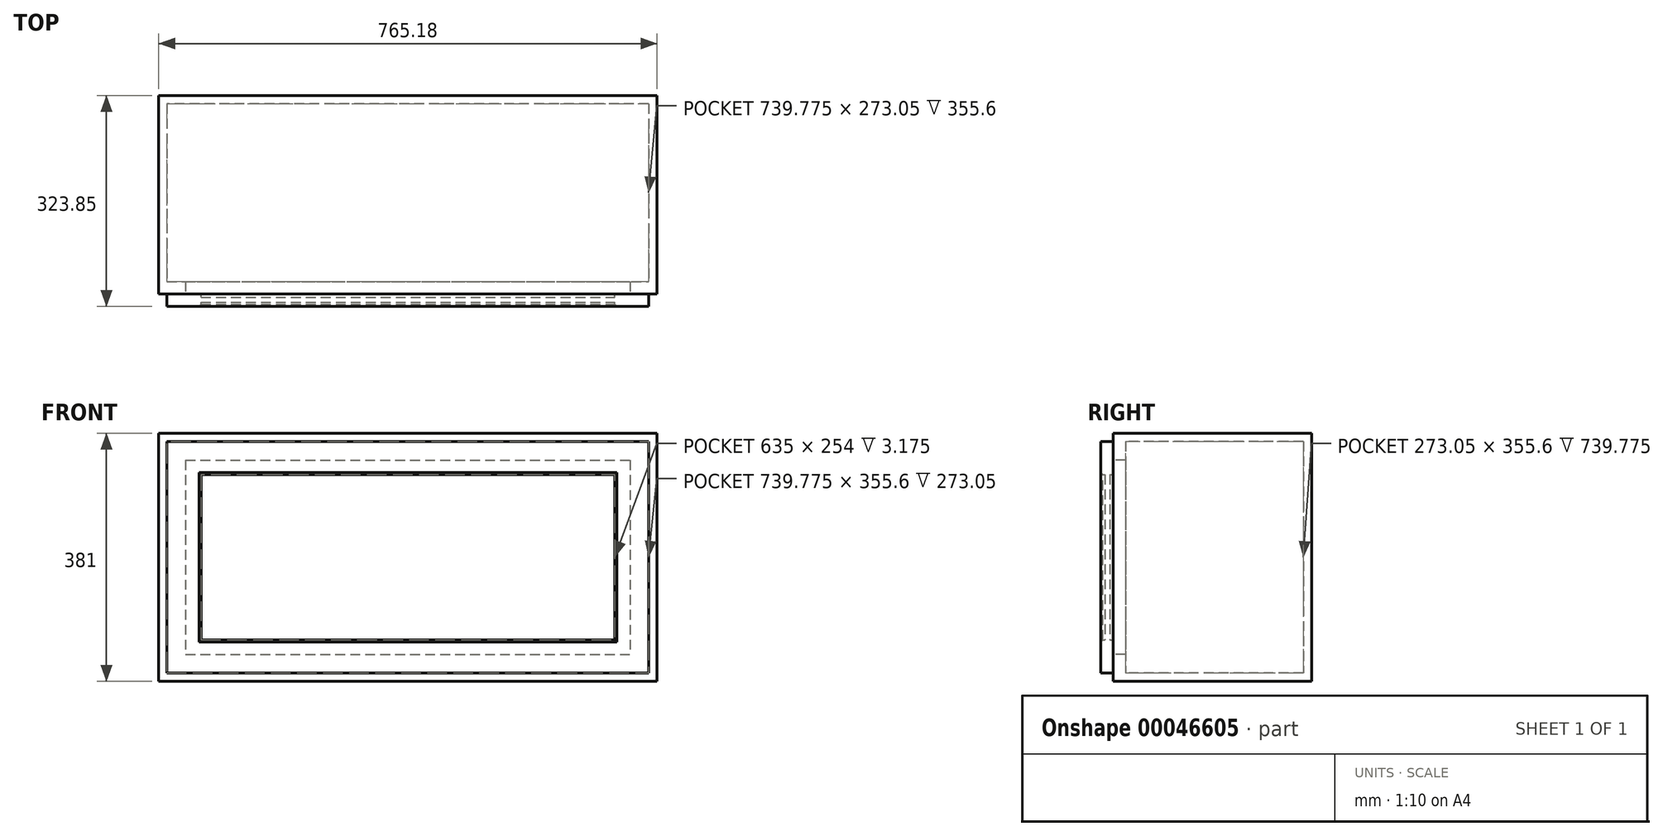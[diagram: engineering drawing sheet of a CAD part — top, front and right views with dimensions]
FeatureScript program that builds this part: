
annotation { "Feature Type Name" : "Feature", "Feature Type Description" : "" }
export const myFeature = defineFeature(function(context is Context, id is Id, definition is map)
    precondition{}
    {
        {
            var Q0;
            Q0=qCreatedBy(makeId("Top.planeOp"),FACE);
            var sketch = newSketch(context, id + "F0", { "sketchPlane" : qUnion([Q0])});
            skLineSegment(sketch, "E0.rect.bottom", {"start": v(382.59, 152.4) * mm, "end": v(-382.59, 152.4) * mm});
            skLineSegment(sketch, "E0.rect.top", {"start": v(382.59, -152.4) * mm, "end": v(-382.59, -152.4) * mm});
            skLineSegment(sketch, "E0.rect.left", {"start": v(382.59, 152.4) * mm, "end": v(382.59, -152.4) * mm});
            skLineSegment(sketch, "E0.rect.right", {"start": v(-382.59, 152.4) * mm, "end": v(-382.59, -152.4) * mm});
            skPoint(sketch, "E0.rect.middle", {"position": v(0, 0) * mm});
            skSolve(sketch);
        }
        {
            var Q0;
            Q0=qSketchRegion(id+"F0",true);
            extrude(context, id + "F1", {"entities" : qUnion([Q0]), "depth" : 381 * mm});
        }
        {
            var Q0;
            Q0=makeQuery(id+"F1.opExtrude","SWEPT_FACE",FACE,{"disambiguationData":[OSD([sQuery(id+"F0.wireOp",EDGE,"E0.rect.top")])]});
            shell(context, id + "F2", {"entities" : qUnion([Q0]), "thickness" : 12.7 * mm});
        }
        {
            var Q0;
            Q0=makeQuery(id+"F1.opExtrude","SWEPT_FACE",FACE,{"disambiguationData":[OSD([sQuery(id+"F0.wireOp",EDGE,"E0.rect.top")])]});
            var sketch = newSketch(context, id + "F3", { "sketchPlane" : qUnion([Q0])});
            skLineSegment(sketch, "E1", {"start": v(-382.59, 0) * mm, "end": v(382.59, 381) * mm, "construction": true});
            skLineSegment(sketch, "E2.rect.bottom", {"start": v(-317.5, 317.5) * mm, "end": v(317.5, 317.5) * mm});
            skLineSegment(sketch, "E2.rect.top", {"start": v(-317.5, 63.5) * mm, "end": v(317.5, 63.5) * mm});
            skLineSegment(sketch, "E2.rect.left", {"start": v(-317.5, 317.5) * mm, "end": v(-317.5, 63.5) * mm});
            skLineSegment(sketch, "E2.rect.right", {"start": v(317.5, 317.5) * mm, "end": v(317.5, 63.5) * mm});
            skPoint(sketch, "E2.rect.middle", {"position": v(0, 190.5) * mm});
            skLineSegment(sketch, "E3.rect.bottom", {"start": v(-341.31, 339.72) * mm, "end": v(341.31, 339.72) * mm});
            skLineSegment(sketch, "E3.rect.top", {"start": v(-341.31, 41.28) * mm, "end": v(341.31, 41.28) * mm});
            skLineSegment(sketch, "E3.rect.left", {"start": v(-341.31, 339.72) * mm, "end": v(-341.31, 41.28) * mm});
            skLineSegment(sketch, "E3.rect.right", {"start": v(341.31, 339.72) * mm, "end": v(341.31, 41.28) * mm});
            skLineSegment(sketch, "E4.rect.bottom", {"start": v(-382.59, 381) * mm, "end": v(382.59, 381) * mm});
            skLineSegment(sketch, "E4.rect.top", {"start": v(-382.59, 0) * mm, "end": v(382.59, 0) * mm});
            skLineSegment(sketch, "E4.rect.left", {"start": v(-382.59, 381) * mm, "end": v(-382.59, 0) * mm});
            skLineSegment(sketch, "E4.rect.right", {"start": v(382.59, 381) * mm, "end": v(382.59, 0) * mm});
            skLineSegment(sketch, "E5.rect.bottom", {"start": v(-374.65, 374.65) * mm, "end": v(374.65, 374.65) * mm});
            skLineSegment(sketch, "E5.rect.top", {"start": v(-374.65, 6.35) * mm, "end": v(374.65, 6.35) * mm});
            skLineSegment(sketch, "E5.rect.left", {"start": v(-374.65, 374.65) * mm, "end": v(-374.65, 6.35) * mm});
            skLineSegment(sketch, "E5.rect.right", {"start": v(374.65, 374.65) * mm, "end": v(374.65, 6.35) * mm});
            skSolve(sketch);
        }
        {
            var Q0;
            Q0=makeQuery(id+"F3.imprint","IMPRINT",FACE,{"disambiguationData":[TD([[makeQuery(id+"F3.imprint","IMPRINT",EDGE,{"derivedFrom":sQuery(id+"F3.wireOp",EDGE,"E4.rect.bottom")}),1.0]])]});
            var Q1;
            Q1=makeQuery(id+"F3.imprint","IMPRINT",FACE,{"disambiguationData":[TD([[makeQuery(id+"F3.imprint","IMPRINT",EDGE,{"derivedFrom":sQuery(id+"F3.wireOp",EDGE,"E5.rect.bottom")}),-1.0]])]});
            var Q2;
            Q2=makeQuery(id+"F3.imprint","IMPRINT",FACE,{"disambiguationData":[TD([[makeQuery(id+"F3.imprint","IMPRINT",EDGE,{"derivedFrom":sQuery(id+"F3.wireOp",EDGE,"E3.rect.bottom")}),1.0]])]});
            extrude(context, id + "F4", {"entities" : qUnion([Q0, Q1, Q2]), "operationType" : NewBodyOperationType.ADD, "oppositeDirection" : true, "depth" : 19.05 * mm});
        }
        {
            var Q0;
            Q0=makeQuery(id+"F3.imprint","IMPRINT",FACE,{"disambiguationData":[TD([[makeQuery(id+"F3.imprint","IMPRINT",EDGE,{"derivedFrom":sQuery(id+"F3.wireOp",EDGE,"E3.rect.bottom")}),1.0]])]});
            var Q1;
            Q1=makeQuery(id+"F3.imprint","IMPRINT",FACE,{"disambiguationData":[TD([[makeQuery(id+"F3.imprint","IMPRINT",EDGE,{"derivedFrom":sQuery(id+"F3.wireOp",EDGE,"E2.rect.bottom")}),1.0]])]});
            extrude(context, id + "F5", {"entities" : qUnion([Q0, Q1]), "operationType" : NewBodyOperationType.ADD, "depth" : 19.05 * mm});
        }
        {
            var Q0;
            Q0=makeQuery(id+"F5.opExtrude","SWEPT_FACE",FACE,{"disambiguationData":[OSD([sQuery(id+"F3.wireOp",EDGE,"E2.rect.right")])]});
            var sketch = newSketch(context, id + "F6", { "sketchPlane" : qUnion([Q0])});
            skLineSegment(sketch, "E6.bottom", {"start": v(157.16, 63.5) * mm, "end": v(165.1, 63.5) * mm});
            skLineSegment(sketch, "E6.top", {"start": v(157.16, 317.5) * mm, "end": v(165.1, 317.5) * mm});
            skLineSegment(sketch, "E6.left", {"start": v(157.16, 63.5) * mm, "end": v(157.16, 317.5) * mm});
            skLineSegment(sketch, "E6.right", {"start": v(165.1, 63.5) * mm, "end": v(165.1, 317.5) * mm});
            skSolve(sketch);
        }
        {
            var Q0;
            Q0=qSketchRegion(id+"F6",true);
            extrude(context, id + "F7", {"entities" : qUnion([Q0]), "operationType" : NewBodyOperationType.ADD, "endBound" : BoundingType.UP_TO_NEXT, "depth" : 25.4 * mm});
        }
        {
            var Q0;
            Q0=makeQuery(id+"F5.opExtrude","CAP_EDGE",EDGE,{"disambiguationData":[OSD([sQuery(id+"F3.wireOp",EDGE,"E2.rect.top")])],"isStart":false});
            var Q1;
            Q1=makeQuery(id+"F5.opExtrude","CAP_EDGE",EDGE,{"disambiguationData":[OSD([sQuery(id+"F3.wireOp",EDGE,"E2.rect.left")])],"isStart":false});
            var Q2;
            Q2=makeQuery(id+"F5.opExtrude","CAP_EDGE",EDGE,{"disambiguationData":[OSD([sQuery(id+"F3.wireOp",EDGE,"E2.rect.bottom")])],"isStart":false});
            var Q3;
            Q3=makeQuery(id+"F5.opExtrude","CAP_EDGE",EDGE,{"disambiguationData":[OSD([sQuery(id+"F3.wireOp",EDGE,"E2.rect.right")])],"isStart":false});
            chamfer(context, id + "F8", {"entities" : qUnion([Q0, Q1, Q2, Q3]), "width" : 3.17 * mm, "tangentPropagation" : true});
        }
    });
